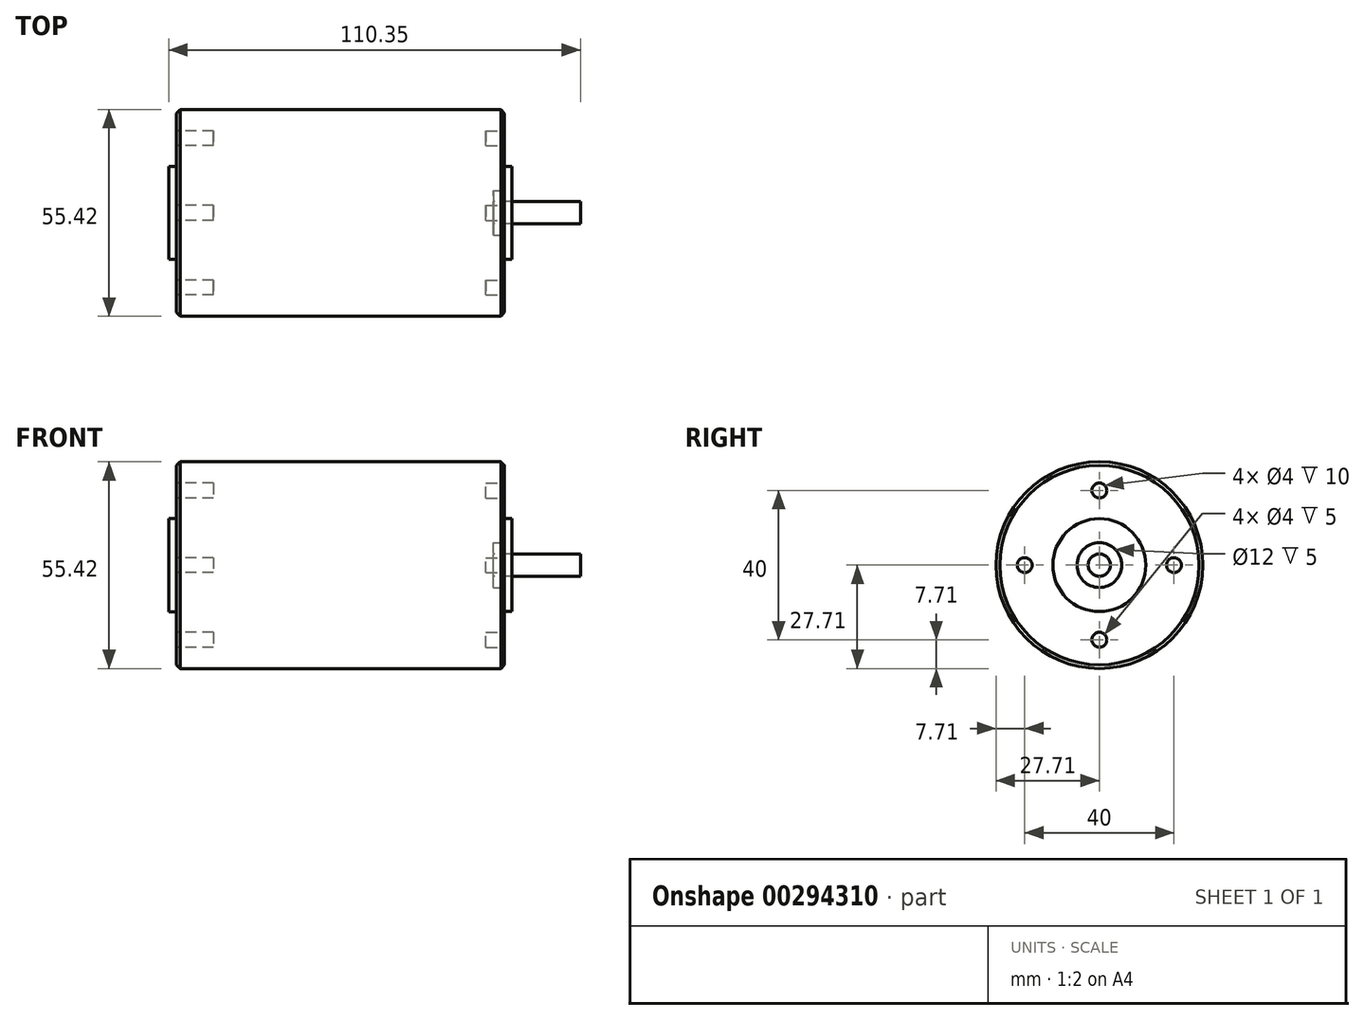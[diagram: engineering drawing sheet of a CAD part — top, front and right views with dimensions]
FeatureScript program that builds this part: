
annotation { "Feature Type Name" : "Feature", "Feature Type Description" : "" }
export const myFeature = defineFeature(function(context is Context, id is Id, definition is map)
    precondition{}
    {
        {
            var Q0;
            Q0=qCreatedBy(makeId("Front.planeOp"),FACE);
            var sketch = newSketch(context, id + "F0", { "sketchPlane" : qUnion([Q0])});
            skLineSegment(sketch, "E0", {"start": v(-46.6, 0) * mm, "end": v(-46.6, 27.7) * mm});
            skLineSegment(sketch, "E1", {"start": v(-46.6, 27.7) * mm, "end": v(41.4, 27.7) * mm});
            skLineSegment(sketch, "E2", {"start": v(41.4, 27.7) * mm, "end": v(41.4, 0) * mm});
            skLineSegment(sketch, "E3", {"start": v(41.4, 0) * mm, "end": v(-46.6, 0) * mm});
            skSolve(sketch);
        }
        {
            var Q0;
            Q0 = qSketchRegion(id + "F0", true);
            var Q1;
            Q1=sQuery(id+"F0.wireOp",EDGE,"E3");
            revolve(context, id + "F1", {"entities" : qUnion([Q0]), "axis" : qUnion([Q1]), "revolveType" : RevolveType.FULL});
        }
        {
            var Q0;
            Q0=makeQuery(id+"F1.opRevolve","SWEPT_EDGE",EDGE,{"disambiguationData":[OSD([sQuery(id+"F0.wireOp",EDGE,"E0"),sQuery(id+"F0.wireOp",EDGE,"E1")])]});
            var Q1;
            Q1=makeQuery(id+"F1.opRevolve","SWEPT_EDGE",EDGE,{"disambiguationData":[OSD([sQuery(id+"F0.wireOp",EDGE,"E1"),sQuery(id+"F0.wireOp",EDGE,"E2")])]});
            chamfer(context, id + "F2", {"entities" : qUnion([Q0, Q1]), "width" : 1 * mm, "tangentPropagation" : true});
        }
        {
            var Q0;
            Q0=makeQuery(id+"F1.opRevolve","SWEPT_FACE",FACE,{"disambiguationData":[OSD([sQuery(id+"F0.wireOp",EDGE,"E2")])]});
            var sketch = newSketch(context, id + "F3", { "sketchPlane" : qUnion([Q0])});
            skCircle(sketch, "E4", {"center": v(0, 0) * mm, "radius": 12.45 * mm});
            skSolve(sketch);
        }
        {
            var Q0;
            Q0 = qSketchRegion(id + "F3", true);
            extrude(context, id + "F4", {"entities" : qUnion([Q0]), "operationType" : NewBodyOperationType.ADD, "depth" : 2 * mm});
        }
        {
            var Q0;
            Q0=makeQuery(id+"F1.opRevolve","SWEPT_FACE",FACE,{"disambiguationData":[OSD([sQuery(id+"F0.wireOp",EDGE,"E0")])]});
            var sketch = newSketch(context, id + "F5", { "sketchPlane" : qUnion([Q0])});
            skCircle(sketch, "E5", {"center": v(0, 0) * mm, "radius": 12.46 * mm});
            skSolve(sketch);
        }
        {
            var Q0;
            Q0=makeQuery(id+"F5.imprint","IMPRINT",FACE,{"disambiguationData":[TD([[makeQuery(id+"F5.imprint","IMPRINT",EDGE,{"derivedFrom":sQuery(id+"F5.wireOp",EDGE,"E5")}),1.0]])]});
            extrude(context, id + "F6", {"entities" : qUnion([Q0]), "operationType" : NewBodyOperationType.ADD, "depth" : 2 * mm});
        }
        {
            var Q0;
            Q0=makeQuery(id+"F1.opRevolve","SWEPT_FACE",FACE,{"disambiguationData":[OSD([sQuery(id+"F0.wireOp",EDGE,"E0")])]});
            var sketch = newSketch(context, id + "F7", { "sketchPlane" : qUnion([Q0])});
            skCircle(sketch, "E6", {"center": v(0, 20) * mm, "radius": 2 * mm});
            skCircle(sketch, "E7.1.0", {"center": v(-20, 0) * mm, "radius": 2 * mm});
            skCircle(sketch, "E7.2.0", {"center": v(0, -20) * mm, "radius": 2 * mm});
            skPoint(sketch, "E7.center", {"position": v(0, 0) * mm});
            skCircle(sketch, "E8.1.3.0", {"center": v(20, 0) * mm, "radius": 2 * mm});
            skSolve(sketch);
        }
        {
            var Q0;
            Q0 = qSketchRegion(id + "F7", true);
            extrude(context, id + "F8", {"entities" : qUnion([Q0]), "operationType" : NewBodyOperationType.REMOVE, "oppositeDirection" : true, "depth" : 10 * mm});
        }
        {
            var Q0;
            Q0=makeQuery(id+"F4.opExtrude","CAP_FACE",FACE,{"disambiguationData":[OSD([sQuery(id+"F3.wireOp",EDGE,"E4")])],"isStart":false});
            var sketch = newSketch(context, id + "F9", { "sketchPlane" : qUnion([Q0])});
            skCircle(sketch, "E9", {"center": v(0, 0) * mm, "radius": 6 * mm});
            skSolve(sketch);
        }
        {
            var Q0;
            Q0 = qSketchRegion(id + "F9", true);
            extrude(context, id + "F10", {"entities" : qUnion([Q0]), "operationType" : NewBodyOperationType.REMOVE, "oppositeDirection" : true, "depth" : 5 * mm});
        }
        {
            var Q0;
            Q0=makeQuery(id+"F10.boolean.opBoolean","COPY",FACE,{"derivedFrom":makeQuery(id+"F10.opExtrude","CAP_FACE",FACE,{"disambiguationData":[OSD([sQuery(id+"F9.wireOp",EDGE,"E9")])],"isStart":false})});
            var sketch = newSketch(context, id + "F11", { "sketchPlane" : qUnion([Q0])});
            skCircle(sketch, "E10", {"center": v(0, 0) * mm, "radius": 2.98 * mm});
            skSolve(sketch);
        }
        {
            var Q0;
            Q0 = qSketchRegion(id + "F11", true);
            extrude(context, id + "F12", {"entities" : qUnion([Q0]), "operationType" : NewBodyOperationType.ADD, "depth" : 23.35 * mm});
        }
        {
            var Q0;
            Q0=makeQuery(id+"F1.opRevolve","SWEPT_FACE",FACE,{"disambiguationData":[OSD([sQuery(id+"F0.wireOp",EDGE,"E2")])]});
            var sketch = newSketch(context, id + "F13", { "sketchPlane" : qUnion([Q0])});
            skCircle(sketch, "E11.0", {"center": v(0, 20) * mm, "radius": 2 * mm});
            skCircle(sketch, "E12.0", {"center": v(20, 0) * mm, "radius": 2 * mm});
            skCircle(sketch, "E13.0", {"center": v(0, -20) * mm, "radius": 2 * mm});
            skCircle(sketch, "E14.0", {"center": v(-20, 0) * mm, "radius": 2 * mm});
            skSolve(sketch);
        }
        {
            var Q0;
            Q0 = qSketchRegion(id + "F13", true);
            extrude(context, id + "F14", {"entities" : qUnion([Q0]), "operationType" : NewBodyOperationType.REMOVE, "oppositeDirection" : true, "depth" : 5 * mm});
        }
    });
